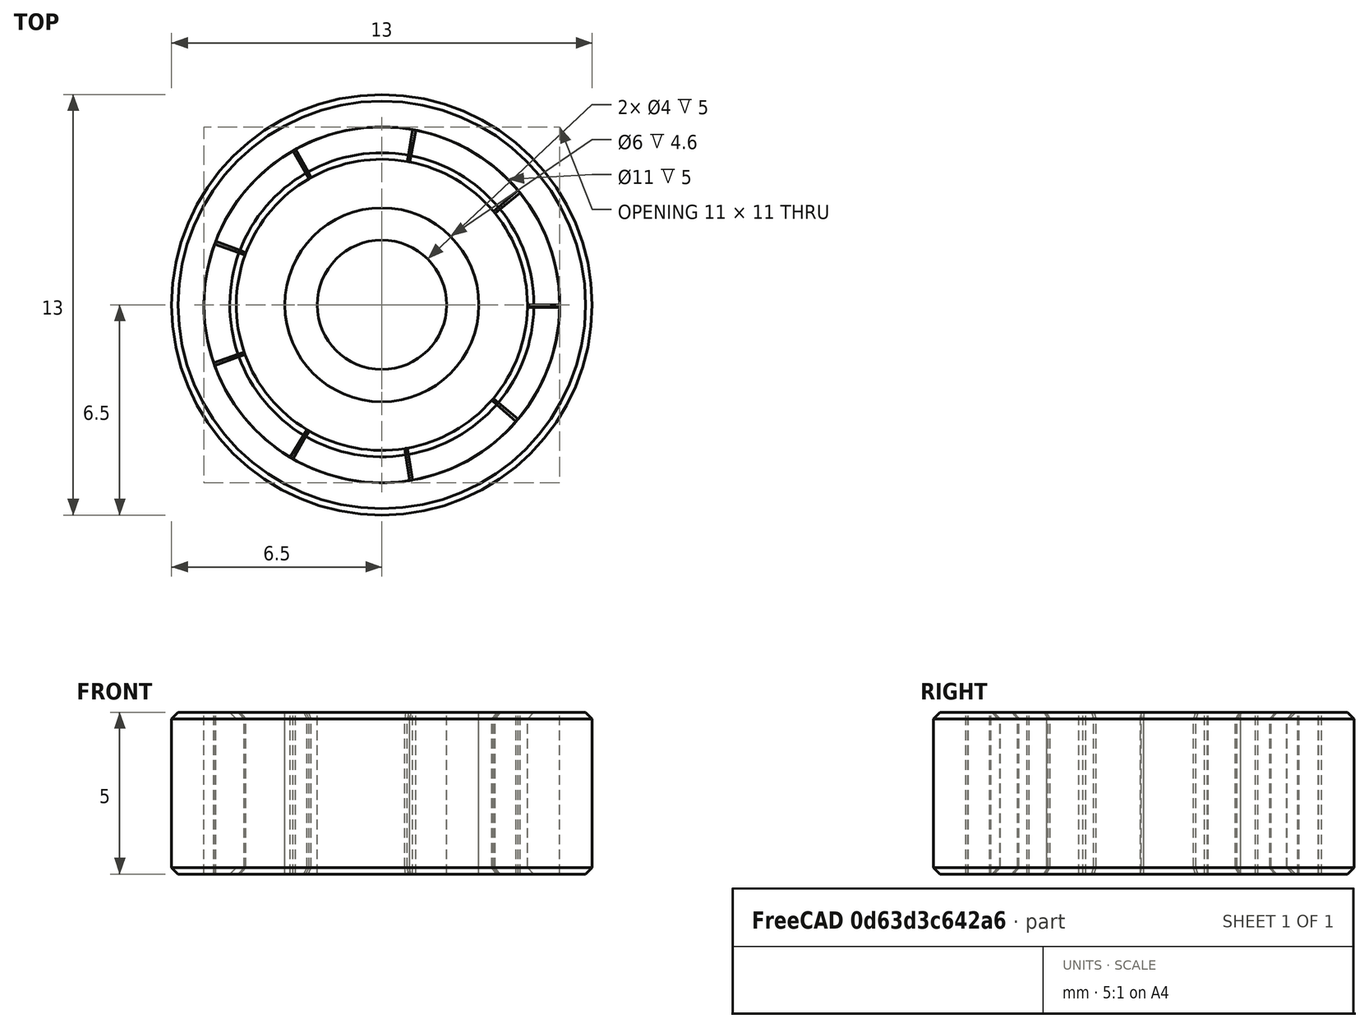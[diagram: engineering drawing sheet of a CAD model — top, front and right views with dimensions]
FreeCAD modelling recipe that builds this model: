
FCSTD DOCUMENT  (FreeCAD 0.14R3702 (Git))
Label: 624zz
License: CC-BY 3.0
LicenseURL: http://creativecommons.org/licenses/by/3.0/
objects: Part::Cylinder×8, Part::Cut×4, Part::Chamfer×2, Part::FeaturePython×1, Part::MultiFuse×1, Part::Feature×1
note: 17 computed .brp shape members not serialized (recipe doc carries the construction recipe); baked Part::Feature solids carry a one-line shape summary decoded from their .brp

FEATURE [Part::Cylinder] Cylinder  label="Exterior"
  Angle = 360
  Height = 5
  Radius = 6.5
FEATURE [Part::Cylinder] Cylinder001  label="Interior"
  Angle = 360
  Height = 5
  Radius = 2
FEATURE [Part::Cylinder] Cylinder002  label="Cilindro"
  Angle = 360
  Height = 5
  Radius = 5.5
FEATURE [Part::Cut] Cut
  Base = -> Cylinder
  Tool = -> Cylinder002
FEATURE [Part::Chamfer] Chamfer  label="Exterior001"
  Base = -> Cut
  Edges = 2 edges r=0.2: [Edge1,Edge3]
FEATURE [Part::Cylinder] Cylinder003  label="Cilindro001"
  Angle = 360
  Height = 5
  Radius = 3
FEATURE [Part::Cut] Cut001  label="Interior001"
  Base = -> Cylinder003
  Tool = -> Cylinder001
FEATURE [Part::Cylinder] Cylinder004  label="Cilindro002"
  Angle = 39
  Height = 5
  Radius = 5.5
FEATURE [Part::Cylinder] Cylinder005  label="Cilindro003"
  Angle = 39
  Height = 5
  Radius = 4.5
FEATURE [Part::Cut] Cut002
  Base = -> Cylinder004
  Tool = -> Cylinder005
FEATURE [Part::Chamfer] Chamfer001
  Base = -> Cut002
  Edges = 2 edges r=0.2: [Edge6,Edge11]
FEATURE [Part::FeaturePython] Array  # Draft array (typed FeaturePython)
  Angle = 360
  ArrayType = 1
  Axis = (0,0,1)
  Base = -> Chamfer001
  Center = (0,0,0)
  IntervalX = (1,0,0)
  IntervalY = (0,1,0)
  IntervalZ = (0,0,1)
  NumberPolar = 9
  NumberX = 2
  NumberY = 2
  NumberZ = 1
FEATURE [Part::Cylinder] Cylinder006  label="Cilindro004"
  Angle = 360
  Height = 4.6
  Placement = pos=(0,0,0.2) rot=(0,0,1;0rad)
  Radius = 4.5
FEATURE [Part::Cylinder] Cylinder007  label="Cilindro005"
  Angle = 360
  Height = 4.6
  Placement = pos=(0,0,0.2) rot=(0,0,1;0rad)
  Radius = 3
FEATURE [Part::Cut] Cut003
  Base = -> Cylinder006
  Tool = -> Cylinder007
FEATURE [Part::MultiFuse] Fusion  label="Medio"
  Shapes = -> [Array,Cut003]
FEATURE [Part::Feature] Fusion002001  label="624zz"
  shape: bbox 13 x 13 x 5 mm, 84 faces (baked)
